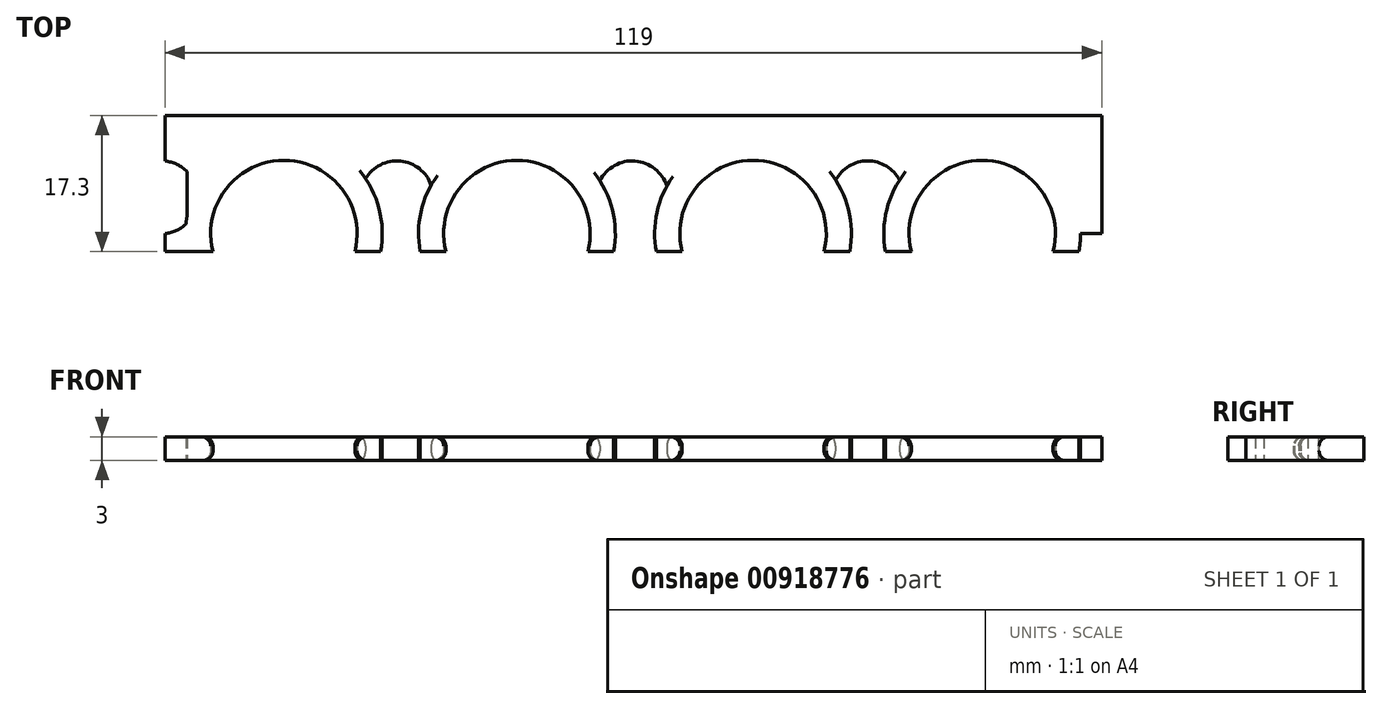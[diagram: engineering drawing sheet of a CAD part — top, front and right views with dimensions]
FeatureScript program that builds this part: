
annotation { "Feature Type Name" : "Feature", "Feature Type Description" : "" }
export const myFeature = defineFeature(function(context is Context, id is Id, definition is map)
    precondition{}
    {
        {
            var Q0;
            Q0=qCreatedBy(makeId("Top.planeOp"),FACE);
            var sketch = newSketch(context, id + "F0", { "sketchPlane" : qUnion([Q0])});
            skLineSegment(sketch, "E0.bottom", {"start": v(59.5, -15) * mm, "end": v(-59.5, -15) * mm});
            skLineSegment(sketch, "E0.top", {"start": v(59.5, 15) * mm, "end": v(-59.5, 15) * mm});
            skLineSegment(sketch, "E0.left", {"start": v(59.5, -15) * mm, "end": v(59.5, 15) * mm});
            skLineSegment(sketch, "E0.right", {"start": v(-59.5, -15) * mm, "end": v(-59.5, 15) * mm});
            skPoint(sketch, "E0.middle", {"position": v(0, 0) * mm});
            skLineSegment(sketch, "E1", {"start": v(-59.5, 0) * mm, "end": v(-57.9, 0) * mm});
            skLineSegment(sketch, "E2", {"start": v(-57.9, 0) * mm, "end": v(-44.4, 0) * mm});
            skLineSegment(sketch, "E3", {"start": v(-44.4, 0) * mm, "end": v(-30.9, 0) * mm});
            skLineSegment(sketch, "E4", {"start": v(-30.9, 0) * mm, "end": v(-29.3, 0) * mm});
            skLineSegment(sketch, "E5", {"start": v(-29.3, 0) * mm, "end": v(-14.8, 0) * mm});
            skLineSegment(sketch, "E6", {"start": v(-14.8, 0) * mm, "end": v(-0.3, 0) * mm});
            skLineSegment(sketch, "E7", {"start": v(-0.3, 0) * mm, "end": v(1.3, 0) * mm});
            skLineSegment(sketch, "E8", {"start": v(1.3, 0) * mm, "end": v(15.2, 0) * mm});
            skLineSegment(sketch, "E9", {"start": v(15.2, 0) * mm, "end": v(29.5, 0) * mm});
            skLineSegment(sketch, "E10", {"start": v(29.5, 0) * mm, "end": v(31.1, 0) * mm});
            skLineSegment(sketch, "E11", {"start": v(31.1, 0) * mm, "end": v(44.3, 0) * mm});
            skLineSegment(sketch, "E12", {"start": v(44.3, 0) * mm, "end": v(57.5, 0) * mm});
            skLineSegment(sketch, "E13", {"start": v(57.5, 0) * mm, "end": v(59.5, 0) * mm});
            skArc(sketch, "E14", {"start": v(-35.39, -2.3) * mm, "mid": v(-44.4, 9.3) * mm, "end": v(-53.41, -2.3) * mm});
            skArc(sketch, "E15", {"start": v(-5.79, -2.3) * mm, "mid": v(-14.8, 9.3) * mm, "end": v(-23.81, -2.3) * mm});
            skArc(sketch, "E16", {"start": v(24.21, -2.3) * mm, "mid": v(15.2, 9.3) * mm, "end": v(6.19, -2.3) * mm});
            skArc(sketch, "E17", {"start": v(53.31, -2.3) * mm, "mid": v(44.3, 9.3) * mm, "end": v(35.29, -2.3) * mm});
            skPoint(sketch, "E18", {"position": v(-59.5, -2.3) * mm});
            skLineSegment(sketch, "E19", {"start": v(-59.5, -2.3) * mm, "end": v(59.5, -2.3) * mm});
            skArc(sketch, "E20", {"start": v(27.49, -2.3) * mm, "mid": v(15.2, 12.5) * mm, "end": v(2.91, -2.3) * mm});
            skArc(sketch, "E21", {"start": v(-2.51, -2.3) * mm, "mid": v(-14.8, 12.5) * mm, "end": v(-27.09, -2.3) * mm});
            skArc(sketch, "E22", {"start": v(56.59, -2.3) * mm, "mid": v(44.3, 12.5) * mm, "end": v(32.01, -2.3) * mm});
            skArc(sketch, "E23", {"start": v(-32.11, -2.3) * mm, "mid": v(-44.4, 12.5) * mm, "end": v(-56.69, -2.3) * mm});
            skLineSegment(sketch, "E24", {"start": v(-56.69, -2.3) * mm, "end": v(-56.69, 7.89) * mm});
            skLineSegment(sketch, "E25", {"start": v(-56.69, 15) * mm, "end": v(-32.11, 15) * mm});
            skLineSegment(sketch, "E26", {"start": v(-27.09, -2.3) * mm, "end": v(-27.09, 2.3) * mm});
            skLineSegment(sketch, "E27", {"start": v(-27.09, 15) * mm, "end": v(-2.51, 15) * mm});
            skLineSegment(sketch, "E28", {"start": v(2.91, -2.3) * mm, "end": v(2.91, 2.3) * mm});
            skLineSegment(sketch, "E29", {"start": v(2.91, 15) * mm, "end": v(27.49, 15) * mm});
            skLineSegment(sketch, "E30", {"start": v(32.01, -2.3) * mm, "end": v(32.01, 2.3) * mm});
            skLineSegment(sketch, "E31", {"start": v(32.01, 15) * mm, "end": v(56.59, 15) * mm});
            skLineSegment(sketch, "E32", {"start": v(56.59, 15) * mm, "end": v(56.59, -2.3) * mm});
            skArc(sketch, "E33", {"start": v(27.49, 0.59) * mm, "mid": v(29.75, 0) * mm, "end": v(32.01, 0.59) * mm});
            skPoint(sketch, "E33.first.point", {"position": v(27.49, 8.64) * mm});
            skPoint(sketch, "E33.second.point", {"position": v(32.01, 8.64) * mm});
            skArc(sketch, "E34.1.0.0", {"start": v(-2.51, 0.64) * mm, "mid": v(0.28, 0.01) * mm, "end": v(2.91, 1.15) * mm});
            skArc(sketch, "E34.2.0.0", {"start": v(-32.11, 0.48) * mm, "mid": v(-29.51, 0.02) * mm, "end": v(-27.09, 1.07) * mm});
            skArc(sketch, "E34.3.0.0", {"start": v(-59.5, 0.02) * mm, "mid": v(-57.98, 0.43) * mm, "end": v(-56.69, 1.34) * mm});
            skLineSegment(sketch, "E34.direction1", {"start": v(29.75, 4.62) * mm, "end": v(-0.15, 4.62) * mm, "construction": true});
            skArc(sketch, "E35.trimOffspring", {"start": v(-56.69, 7.89) * mm, "mid": v(-57.98, 8.8) * mm, "end": v(-59.5, 9.22) * mm});
            skLineSegment(sketch, "E36.trimOffspring", {"start": v(-32.11, 2.3) * mm, "end": v(-32.11, -2.3) * mm});
            skArc(sketch, "E37.trimOffspring", {"start": v(-25.69, 6.14) * mm, "mid": v(-29.6, 9.21) * mm, "end": v(-34.03, 6.97) * mm});
            skLineSegment(sketch, "E38.trimOffspring", {"start": v(-2.51, 2.3) * mm, "end": v(-2.51, -2.3) * mm});
            skArc(sketch, "E39.trimOffspring", {"start": v(4.25, 6.03) * mm, "mid": v(0.23, 9.22) * mm, "end": v(-4.26, 6.72) * mm});
            skLineSegment(sketch, "E40.trimOffspring", {"start": v(27.49, 2.3) * mm, "end": v(27.49, -2.3) * mm});
            skArc(sketch, "E41.trimOffspring", {"start": v(33.82, 6.8) * mm, "mid": v(29.75, 9.24) * mm, "end": v(25.68, 6.8) * mm});
            skSolve(sketch);
        }
        {
            var Q0;
            {var subQ18=sQuery(id+"F0.wireOp",EDGE,"E0.top");Q0=makeQuery(id+"F0.imprint","IMPRINT",FACE,{"disambiguationData":[TD([[makeQuery(id+"F0.imprint","IMPRINT",EDGE,{"derivedFrom":subQ18}),1.0]])]});}
            var Q1;
            {var subQ0=sQuery(id+"F0.wireOp",EDGE,"E23");var subQ1=sQuery(id+"F0.wireOp",EDGE,"E2");var subQ2=makeQuery(id+"F0.imprint","INTERSECT",VERTEX,{"derivedFrom":[subQ1,subQ0]});Q1=makeQuery(id+"F0.imprint","IMPRINT",FACE,{"disambiguationData":[TD([[makeQuery(id+"F0.imprint","IMPRINT",EDGE,{"disambiguationData":[TD([[subQ2,-1.0]])],"derivedFrom":subQ1}),1.0]])]});}
            var Q2;
            {var subQ0=sQuery(id+"F0.wireOp",EDGE,"E23");var subQ1=sQuery(id+"F0.wireOp",EDGE,"E2");var subQ2=makeQuery(id+"F0.imprint","INTERSECT",VERTEX,{"derivedFrom":[subQ1,subQ0]});Q2=makeQuery(id+"F0.imprint","IMPRINT",FACE,{"disambiguationData":[TD([[makeQuery(id+"F0.imprint","IMPRINT",EDGE,{"disambiguationData":[TD([[subQ2,-1.0]])],"derivedFrom":subQ1}),-1.0]])]});}
            var Q3;
            {var subQ0=sQuery(id+"F0.wireOp",EDGE,"E14");var subQ1=sQuery(id+"F0.wireOp",EDGE,"E3");var subQ2=makeQuery(id+"F0.imprint","INTERSECT",VERTEX,{"derivedFrom":[subQ1,subQ0]});Q3=makeQuery(id+"F0.imprint","IMPRINT",FACE,{"disambiguationData":[TD([[makeQuery(id+"F0.imprint","IMPRINT",EDGE,{"disambiguationData":[TD([[subQ2,-1.0]])],"derivedFrom":subQ1}),-1.0]])]});}
            var Q4;
            {var subQ0=sQuery(id+"F0.wireOp",EDGE,"E21");var subQ1=sQuery(id+"F0.wireOp",EDGE,"E5");var subQ2=makeQuery(id+"F0.imprint","INTERSECT",VERTEX,{"derivedFrom":[subQ1,subQ0]});Q4=makeQuery(id+"F0.imprint","IMPRINT",FACE,{"disambiguationData":[TD([[makeQuery(id+"F0.imprint","IMPRINT",EDGE,{"disambiguationData":[TD([[subQ2,-1.0]])],"derivedFrom":subQ1}),-1.0]])]});}
            var Q5;
            {var subQ0=sQuery(id+"F0.wireOp",EDGE,"E21");var subQ1=sQuery(id+"F0.wireOp",EDGE,"E5");var subQ2=makeQuery(id+"F0.imprint","INTERSECT",VERTEX,{"derivedFrom":[subQ1,subQ0]});Q5=makeQuery(id+"F0.imprint","IMPRINT",FACE,{"disambiguationData":[TD([[makeQuery(id+"F0.imprint","IMPRINT",EDGE,{"disambiguationData":[TD([[subQ2,-1.0]])],"derivedFrom":subQ1}),1.0]])]});}
            var Q6;
            {var subQ0=sQuery(id+"F0.wireOp",EDGE,"E15");var subQ1=sQuery(id+"F0.wireOp",EDGE,"E6");var subQ2=makeQuery(id+"F0.imprint","INTERSECT",VERTEX,{"derivedFrom":[subQ1,subQ0]});Q6=makeQuery(id+"F0.imprint","IMPRINT",FACE,{"disambiguationData":[TD([[makeQuery(id+"F0.imprint","IMPRINT",EDGE,{"disambiguationData":[TD([[subQ2,-1.0]])],"derivedFrom":subQ1}),-1.0]])]});}
            var Q7;
            {var subQ0=sQuery(id+"F0.wireOp",EDGE,"E20");var subQ1=sQuery(id+"F0.wireOp",EDGE,"E8");var subQ2=makeQuery(id+"F0.imprint","INTERSECT",VERTEX,{"derivedFrom":[subQ1,subQ0]});Q7=makeQuery(id+"F0.imprint","IMPRINT",FACE,{"disambiguationData":[TD([[makeQuery(id+"F0.imprint","IMPRINT",EDGE,{"disambiguationData":[TD([[subQ2,-1.0]])],"derivedFrom":subQ1}),-1.0]])]});}
            var Q8;
            {var subQ0=sQuery(id+"F0.wireOp",EDGE,"E20");var subQ1=sQuery(id+"F0.wireOp",EDGE,"E8");var subQ2=makeQuery(id+"F0.imprint","INTERSECT",VERTEX,{"derivedFrom":[subQ1,subQ0]});Q8=makeQuery(id+"F0.imprint","IMPRINT",FACE,{"disambiguationData":[TD([[makeQuery(id+"F0.imprint","IMPRINT",EDGE,{"disambiguationData":[TD([[subQ2,-1.0]])],"derivedFrom":subQ1}),1.0]])]});}
            var Q9;
            {var subQ0=sQuery(id+"F0.wireOp",EDGE,"E16");var subQ1=sQuery(id+"F0.wireOp",EDGE,"E9");var subQ2=makeQuery(id+"F0.imprint","INTERSECT",VERTEX,{"derivedFrom":[subQ1,subQ0]});Q9=makeQuery(id+"F0.imprint","IMPRINT",FACE,{"disambiguationData":[TD([[makeQuery(id+"F0.imprint","IMPRINT",EDGE,{"disambiguationData":[TD([[subQ2,-1.0]])],"derivedFrom":subQ1}),-1.0]])]});}
            var Q10;
            {var subQ0=sQuery(id+"F0.wireOp",EDGE,"E22");var subQ1=sQuery(id+"F0.wireOp",EDGE,"E11");var subQ2=makeQuery(id+"F0.imprint","INTERSECT",VERTEX,{"derivedFrom":[subQ1,subQ0]});Q10=makeQuery(id+"F0.imprint","IMPRINT",FACE,{"disambiguationData":[TD([[makeQuery(id+"F0.imprint","IMPRINT",EDGE,{"disambiguationData":[TD([[subQ2,-1.0]])],"derivedFrom":subQ1}),-1.0]])]});}
            var Q11;
            {var subQ0=sQuery(id+"F0.wireOp",EDGE,"E22");var subQ1=sQuery(id+"F0.wireOp",EDGE,"E11");var subQ2=makeQuery(id+"F0.imprint","INTERSECT",VERTEX,{"derivedFrom":[subQ1,subQ0]});Q11=makeQuery(id+"F0.imprint","IMPRINT",FACE,{"disambiguationData":[TD([[makeQuery(id+"F0.imprint","IMPRINT",EDGE,{"disambiguationData":[TD([[subQ2,-1.0]])],"derivedFrom":subQ1}),1.0]])]});}
            var Q12;
            {var subQ0=sQuery(id+"F0.wireOp",EDGE,"E17");var subQ1=sQuery(id+"F0.wireOp",EDGE,"E12");var subQ2=makeQuery(id+"F0.imprint","INTERSECT",VERTEX,{"derivedFrom":[subQ1,subQ0]});Q12=makeQuery(id+"F0.imprint","IMPRINT",FACE,{"disambiguationData":[TD([[makeQuery(id+"F0.imprint","IMPRINT",EDGE,{"disambiguationData":[TD([[subQ2,-1.0]])],"derivedFrom":subQ1}),-1.0]])]});}
            var Q13;
            {var subQ8=sQuery(id+"F0.wireOp",EDGE,"E5");var subQ10=sQuery(id+"F0.wireOp",EDGE,"E26");var subQ11=makeQuery(id+"F0.imprint","INTERSECT",VERTEX,{"derivedFrom":[subQ8,subQ10]});Q13=makeQuery(id+"F0.imprint","IMPRINT",FACE,{"disambiguationData":[TD([[makeQuery(id+"F0.imprint","IMPRINT",EDGE,{"disambiguationData":[TD([[subQ11,-1.0]])],"derivedFrom":subQ8}),1.0]])]});}
            var Q14;
            {var subQ8=sQuery(id+"F0.wireOp",EDGE,"E8");var subQ11=sQuery(id+"F0.wireOp",EDGE,"E28");var subQ14=makeQuery(id+"F0.imprint","INTERSECT",VERTEX,{"derivedFrom":[subQ8,subQ11]});Q14=makeQuery(id+"F0.imprint","IMPRINT",FACE,{"disambiguationData":[TD([[makeQuery(id+"F0.imprint","IMPRINT",EDGE,{"disambiguationData":[TD([[subQ14,-1.0]])],"derivedFrom":subQ8}),1.0]])]});}
            var Q15;
            {var subQ5=sQuery(id+"F0.wireOp",EDGE,"E11");var subQ9=sQuery(id+"F0.wireOp",EDGE,"E30");var subQ11=makeQuery(id+"F0.imprint","INTERSECT",VERTEX,{"derivedFrom":[subQ5,subQ9]});Q15=makeQuery(id+"F0.imprint","IMPRINT",FACE,{"disambiguationData":[TD([[makeQuery(id+"F0.imprint","IMPRINT",EDGE,{"disambiguationData":[TD([[subQ11,-1.0]])],"derivedFrom":subQ5}),1.0]])]});}
            var Q16;
            {var subQ0=sQuery(id+"F0.wireOp",EDGE,"E26");var subQ1=sQuery(id+"F0.wireOp",EDGE,"E5");var subQ2=makeQuery(id+"F0.imprint","INTERSECT",VERTEX,{"derivedFrom":[subQ1,subQ0]});Q16=makeQuery(id+"F0.imprint","IMPRINT",FACE,{"disambiguationData":[TD([[makeQuery(id+"F0.imprint","IMPRINT",EDGE,{"disambiguationData":[TD([[subQ2,-1.0]])],"derivedFrom":subQ1}),-1.0]])]});}
            var Q17;
            {var subQ0=sQuery(id+"F0.wireOp",EDGE,"E28");var subQ1=sQuery(id+"F0.wireOp",EDGE,"E8");var subQ2=makeQuery(id+"F0.imprint","INTERSECT",VERTEX,{"derivedFrom":[subQ1,subQ0]});Q17=makeQuery(id+"F0.imprint","IMPRINT",FACE,{"disambiguationData":[TD([[makeQuery(id+"F0.imprint","IMPRINT",EDGE,{"disambiguationData":[TD([[subQ2,-1.0]])],"derivedFrom":subQ1}),-1.0]])]});}
            var Q18;
            {var subQ0=sQuery(id+"F0.wireOp",EDGE,"E30");var subQ1=sQuery(id+"F0.wireOp",EDGE,"E11");var subQ2=makeQuery(id+"F0.imprint","INTERSECT",VERTEX,{"derivedFrom":[subQ1,subQ0]});Q18=makeQuery(id+"F0.imprint","IMPRINT",FACE,{"disambiguationData":[TD([[makeQuery(id+"F0.imprint","IMPRINT",EDGE,{"disambiguationData":[TD([[subQ2,-1.0]])],"derivedFrom":subQ1}),-1.0]])]});}
            var Q19;
            {var subQ9=sQuery(id+"F0.wireOp",EDGE,"E24");var subQ11=sQuery(id+"F0.wireOp",EDGE,"E2");var subQ12=makeQuery(id+"F0.imprint","INTERSECT",VERTEX,{"derivedFrom":[subQ11,subQ9]});Q19=makeQuery(id+"F0.imprint","IMPRINT",FACE,{"disambiguationData":[TD([[makeQuery(id+"F0.imprint","IMPRINT",EDGE,{"disambiguationData":[TD([[subQ12,-1.0]])],"derivedFrom":subQ11}),1.0]])]});}
            var Q20;
            {var subQ0=sQuery(id+"F0.wireOp",EDGE,"E24");var subQ1=sQuery(id+"F0.wireOp",EDGE,"E2");var subQ2=makeQuery(id+"F0.imprint","INTERSECT",VERTEX,{"derivedFrom":[subQ1,subQ0]});Q20=makeQuery(id+"F0.imprint","IMPRINT",FACE,{"disambiguationData":[TD([[makeQuery(id+"F0.imprint","IMPRINT",EDGE,{"disambiguationData":[TD([[subQ2,-1.0]])],"derivedFrom":subQ1}),-1.0]])]});}
            var Q21;
            {var subQ5=sQuery(id+"F0.wireOp",EDGE,"E1");Q21=makeQuery(id+"F0.imprint","IMPRINT",FACE,{"disambiguationData":[TD([[makeQuery(id+"F0.imprint","IMPRINT",EDGE,{"derivedFrom":subQ5}),-1.0]])]});}
            var Q22;
            {var subQ1=sQuery(id+"F0.wireOp",EDGE,"E1");Q22=makeQuery(id+"F0.imprint","IMPRINT",FACE,{"disambiguationData":[TD([[makeQuery(id+"F0.imprint","IMPRINT",EDGE,{"derivedFrom":subQ1}),1.0]])]});}
            var Q23;
            {var subQ0=sQuery(id+"F0.wireOp",EDGE,"E24");var subQ1=sQuery(id+"F0.wireOp",EDGE,"E23");var subQ2=makeQuery(id+"F0.imprint","INTERSECT",VERTEX,{"derivedFrom":[subQ1,subQ0]});Q23=makeQuery(id+"F0.imprint","IMPRINT",FACE,{"disambiguationData":[TD([[makeQuery(id+"F0.imprint","IMPRINT",EDGE,{"disambiguationData":[TD([[subQ2,-1.0]])],"derivedFrom":subQ1}),1.0]])]});}
            var Q24;
            {var subQ0=sQuery(id+"F0.wireOp",EDGE,"E36.trimOffspring");var subQ1=sQuery(id+"F0.wireOp",EDGE,"E3");var subQ2=makeQuery(id+"F0.imprint","INTERSECT",VERTEX,{"derivedFrom":[subQ1,subQ0]});Q24=makeQuery(id+"F0.imprint","IMPRINT",FACE,{"disambiguationData":[TD([[makeQuery(id+"F0.imprint","IMPRINT",EDGE,{"disambiguationData":[TD([[subQ2,-1.0]])],"derivedFrom":subQ1}),-1.0]])]});}
            var Q25;
            {var subQ0=sQuery(id+"F0.wireOp",EDGE,"E36.trimOffspring");var subQ1=sQuery(id+"F0.wireOp",EDGE,"E3");var subQ2=makeQuery(id+"F0.imprint","INTERSECT",VERTEX,{"derivedFrom":[subQ1,subQ0]});Q25=makeQuery(id+"F0.imprint","IMPRINT",FACE,{"disambiguationData":[TD([[makeQuery(id+"F0.imprint","IMPRINT",EDGE,{"disambiguationData":[TD([[subQ2,-1.0]])],"derivedFrom":subQ1}),1.0]])]});}
            var Q26;
            {var subQ0=sQuery(id+"F0.wireOp",EDGE,"E36.trimOffspring");var subQ1=sQuery(id+"F0.wireOp",EDGE,"E23");var subQ2=makeQuery(id+"F0.imprint","INTERSECT",VERTEX,{"derivedFrom":[subQ1,subQ0]});Q26=makeQuery(id+"F0.imprint","IMPRINT",FACE,{"disambiguationData":[TD([[makeQuery(id+"F0.imprint","IMPRINT",EDGE,{"disambiguationData":[TD([[subQ2,1.0]])],"derivedFrom":subQ1}),1.0]])]});}
            var Q27;
            {var subQ0=sQuery(id+"F0.wireOp",EDGE,"E26");var subQ1=sQuery(id+"F0.wireOp",EDGE,"E21");var subQ2=makeQuery(id+"F0.imprint","INTERSECT",VERTEX,{"derivedFrom":[subQ1,subQ0]});Q27=makeQuery(id+"F0.imprint","IMPRINT",FACE,{"disambiguationData":[TD([[makeQuery(id+"F0.imprint","IMPRINT",EDGE,{"disambiguationData":[TD([[subQ2,-1.0]])],"derivedFrom":subQ1}),1.0]])]});}
            var Q28;
            {var subQ0=sQuery(id+"F0.wireOp",EDGE,"E38.trimOffspring");var subQ1=sQuery(id+"F0.wireOp",EDGE,"E6");var subQ2=makeQuery(id+"F0.imprint","INTERSECT",VERTEX,{"derivedFrom":[subQ1,subQ0]});Q28=makeQuery(id+"F0.imprint","IMPRINT",FACE,{"disambiguationData":[TD([[makeQuery(id+"F0.imprint","IMPRINT",EDGE,{"disambiguationData":[TD([[subQ2,-1.0]])],"derivedFrom":subQ1}),1.0]])]});}
            var Q29;
            {var subQ0=sQuery(id+"F0.wireOp",EDGE,"E38.trimOffspring");var subQ1=sQuery(id+"F0.wireOp",EDGE,"E6");var subQ2=makeQuery(id+"F0.imprint","INTERSECT",VERTEX,{"derivedFrom":[subQ1,subQ0]});Q29=makeQuery(id+"F0.imprint","IMPRINT",FACE,{"disambiguationData":[TD([[makeQuery(id+"F0.imprint","IMPRINT",EDGE,{"disambiguationData":[TD([[subQ2,-1.0]])],"derivedFrom":subQ1}),-1.0]])]});}
            var Q30;
            {var subQ0=sQuery(id+"F0.wireOp",EDGE,"E38.trimOffspring");var subQ1=sQuery(id+"F0.wireOp",EDGE,"E21");var subQ2=makeQuery(id+"F0.imprint","INTERSECT",VERTEX,{"derivedFrom":[subQ1,subQ0]});Q30=makeQuery(id+"F0.imprint","IMPRINT",FACE,{"disambiguationData":[TD([[makeQuery(id+"F0.imprint","IMPRINT",EDGE,{"disambiguationData":[TD([[subQ2,1.0]])],"derivedFrom":subQ1}),1.0]])]});}
            var Q31;
            {var subQ0=sQuery(id+"F0.wireOp",EDGE,"E28");var subQ1=sQuery(id+"F0.wireOp",EDGE,"E20");var subQ2=makeQuery(id+"F0.imprint","INTERSECT",VERTEX,{"derivedFrom":[subQ1,subQ0]});Q31=makeQuery(id+"F0.imprint","IMPRINT",FACE,{"disambiguationData":[TD([[makeQuery(id+"F0.imprint","IMPRINT",EDGE,{"disambiguationData":[TD([[subQ2,-1.0]])],"derivedFrom":subQ1}),1.0]])]});}
            var Q32;
            {var subQ0=sQuery(id+"F0.wireOp",EDGE,"E40.trimOffspring");var subQ1=sQuery(id+"F0.wireOp",EDGE,"E9");var subQ2=makeQuery(id+"F0.imprint","INTERSECT",VERTEX,{"derivedFrom":[subQ1,subQ0]});Q32=makeQuery(id+"F0.imprint","IMPRINT",FACE,{"disambiguationData":[TD([[makeQuery(id+"F0.imprint","IMPRINT",EDGE,{"disambiguationData":[TD([[subQ2,-1.0]])],"derivedFrom":subQ1}),-1.0]])]});}
            var Q33;
            {var subQ0=sQuery(id+"F0.wireOp",EDGE,"E40.trimOffspring");var subQ1=sQuery(id+"F0.wireOp",EDGE,"E9");var subQ2=makeQuery(id+"F0.imprint","INTERSECT",VERTEX,{"derivedFrom":[subQ1,subQ0]});Q33=makeQuery(id+"F0.imprint","IMPRINT",FACE,{"disambiguationData":[TD([[makeQuery(id+"F0.imprint","IMPRINT",EDGE,{"disambiguationData":[TD([[subQ2,-1.0]])],"derivedFrom":subQ1}),1.0]])]});}
            var Q34;
            {var subQ0=sQuery(id+"F0.wireOp",EDGE,"E40.trimOffspring");var subQ1=sQuery(id+"F0.wireOp",EDGE,"E20");var subQ2=makeQuery(id+"F0.imprint","INTERSECT",VERTEX,{"derivedFrom":[subQ1,subQ0]});Q34=makeQuery(id+"F0.imprint","IMPRINT",FACE,{"disambiguationData":[TD([[makeQuery(id+"F0.imprint","IMPRINT",EDGE,{"disambiguationData":[TD([[subQ2,1.0]])],"derivedFrom":subQ1}),1.0]])]});}
            var Q35;
            {var subQ0=sQuery(id+"F0.wireOp",EDGE,"E30");var subQ1=sQuery(id+"F0.wireOp",EDGE,"E22");var subQ2=makeQuery(id+"F0.imprint","INTERSECT",VERTEX,{"derivedFrom":[subQ1,subQ0]});Q35=makeQuery(id+"F0.imprint","IMPRINT",FACE,{"disambiguationData":[TD([[makeQuery(id+"F0.imprint","IMPRINT",EDGE,{"disambiguationData":[TD([[subQ2,-1.0]])],"derivedFrom":subQ1}),1.0]])]});}
            var Q36;
            {var subQ0=sQuery(id+"F0.wireOp",EDGE,"E32");var subQ1=sQuery(id+"F0.wireOp",EDGE,"E12");var subQ2=makeQuery(id+"F0.imprint","INTERSECT",VERTEX,{"derivedFrom":[subQ1,subQ0]});Q36=makeQuery(id+"F0.imprint","IMPRINT",FACE,{"disambiguationData":[TD([[makeQuery(id+"F0.imprint","IMPRINT",EDGE,{"disambiguationData":[TD([[subQ2,-1.0]])],"derivedFrom":subQ1}),-1.0]])]});}
            var Q37;
            {var subQ0=sQuery(id+"F0.wireOp",EDGE,"E32");var subQ1=sQuery(id+"F0.wireOp",EDGE,"E12");var subQ2=makeQuery(id+"F0.imprint","INTERSECT",VERTEX,{"derivedFrom":[subQ1,subQ0]});Q37=makeQuery(id+"F0.imprint","IMPRINT",FACE,{"disambiguationData":[TD([[makeQuery(id+"F0.imprint","IMPRINT",EDGE,{"disambiguationData":[TD([[subQ2,-1.0]])],"derivedFrom":subQ1}),1.0]])]});}
            var Q38;
            {var subQ0=sQuery(id+"F0.wireOp",EDGE,"E13");Q38=makeQuery(id+"F0.imprint","IMPRINT",FACE,{"disambiguationData":[TD([[makeQuery(id+"F0.imprint","IMPRINT",EDGE,{"derivedFrom":subQ0}),1.0]])]});}
            extrude(context, id + "F1", {"entities" : qUnion([Q0, Q1, Q2, Q3, Q4, Q5, Q6, Q7, Q8, Q9, Q10, Q11, Q12, Q13, Q14, Q15, Q16, Q17, Q18, Q19, Q20, Q21, Q22, Q23, Q24, Q25, Q26, Q27, Q28, Q29, Q30, Q31, Q32, Q33, Q34, Q35, Q36, Q37, Q38]), "depth" : 3 * mm, "offsetDistance" : 25 * mm});
        }
        {
            var Q0;
            Q0=makeQuery(id+"F1.opExtrude","CAP_EDGE",EDGE,{"disambiguationData":[OSD([sQuery(id+"F0.wireOp",EDGE,"E15")])],"isStart":false});
            var Q1;
            Q1=makeQuery(id+"F1.opExtrude","CAP_EDGE",EDGE,{"disambiguationData":[OSD([sQuery(id+"F0.wireOp",EDGE,"E14")])],"isStart":false});
            var Q2;
            Q2=makeQuery(id+"F1.opExtrude","CAP_EDGE",EDGE,{"disambiguationData":[OSD([sQuery(id+"F0.wireOp",EDGE,"E16")])],"isStart":false});
            var Q3;
            Q3=makeQuery(id+"F1.opExtrude","CAP_EDGE",EDGE,{"disambiguationData":[OSD([sQuery(id+"F0.wireOp",EDGE,"E17")])],"isStart":false});
            var Q4;
            Q4=makeQuery(id+"F1.opExtrude","CAP_EDGE",EDGE,{"disambiguationData":[OSD([sQuery(id+"F0.wireOp",EDGE,"E16")])],"isStart":true});
            var Q5;
            Q5=makeQuery(id+"F1.opExtrude","CAP_EDGE",EDGE,{"disambiguationData":[OSD([sQuery(id+"F0.wireOp",EDGE,"E14")])],"isStart":true});
            var Q6;
            Q6=makeQuery(id+"F1.opExtrude","CAP_EDGE",EDGE,{"disambiguationData":[OSD([sQuery(id+"F0.wireOp",EDGE,"E15")])],"isStart":true});
            var Q7;
            Q7=makeQuery(id+"F1.opExtrude","CAP_EDGE",EDGE,{"disambiguationData":[OSD([sQuery(id+"F0.wireOp",EDGE,"E17")])],"isStart":true});
            var Q8;
            Q8=makeQuery(id+"F1.opExtrude","CAP_EDGE",EDGE,{"disambiguationData":[OSD([sQuery(id+"F0.wireOp",EDGE,"E39.trimOffspring")])],"isStart":true});
            var Q9;
            Q9=makeQuery(id+"F1.opExtrude","CAP_EDGE",EDGE,{"disambiguationData":[OSD([sQuery(id+"F0.wireOp",EDGE,"E39.trimOffspring")])],"isStart":false});
            var Q10;
            Q10=makeQuery(id+"F1.opExtrude","CAP_EDGE",EDGE,{"disambiguationData":[OSD([sQuery(id+"F0.wireOp",EDGE,"E37.trimOffspring")])],"isStart":true});
            var Q11;
            Q11=makeQuery(id+"F1.opExtrude","CAP_EDGE",EDGE,{"disambiguationData":[OSD([sQuery(id+"F0.wireOp",EDGE,"E37.trimOffspring")])],"isStart":false});
            var Q12;
            Q12=makeQuery(id+"F1.opExtrude","CAP_EDGE",EDGE,{"disambiguationData":[OSD([sQuery(id+"F0.wireOp",EDGE,"E41.trimOffspring")])],"isStart":true});
            var Q13;
            Q13=makeQuery(id+"F1.opExtrude","CAP_EDGE",EDGE,{"disambiguationData":[OSD([sQuery(id+"F0.wireOp",EDGE,"E41.trimOffspring")])],"isStart":false});
            fillet(context, id + "F2", {"entities" : qUnion([Q0, Q1, Q2, Q3, Q4, Q5, Q6, Q7, Q8, Q9, Q10, Q11, Q12, Q13]), "radius" : 1.2 * mm, "tangentPropagation" : true, "allowEdgeOverflow" : false});
        }
    });
